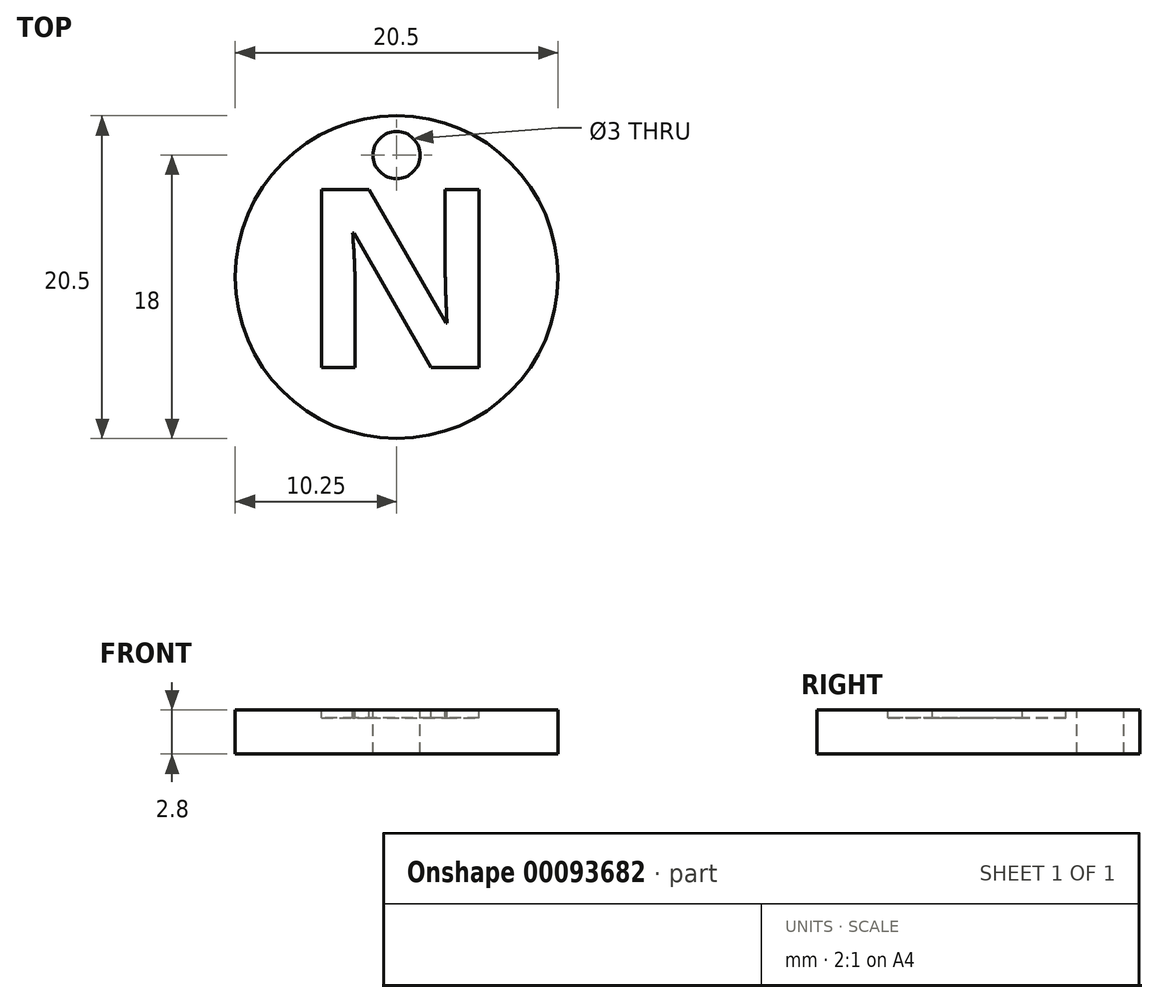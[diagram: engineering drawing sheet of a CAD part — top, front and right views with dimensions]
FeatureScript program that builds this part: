
annotation { "Feature Type Name" : "Feature", "Feature Type Description" : "" }
export const myFeature = defineFeature(function(context is Context, id is Id, definition is map)
    precondition{}
    {
        {
            var Q0;
            Q0=qCreatedBy(makeId("Top.planeOp"),FACE);
            var sketch = newSketch(context, id + "F0", { "sketchPlane" : qUnion([Q0])});
            skCircle(sketch, "E0", {"center": v(0, 0) * mm, "radius": 10.25 * mm});
            skSolve(sketch);
        }
        {
            var Q0;
            Q0=makeQuery(id+"F0.imprint","IMPRINT",FACE,{"disambiguationData":[TD([[makeQuery(id+"F0.imprint","IMPRINT",EDGE,{"derivedFrom":sQuery(id+"F0.wireOp",EDGE,"E0")}),1.0]])]});
            extrude(context, id + "F1", {"entities" : qUnion([Q0]), "depth" : 2.8 * mm});
        }
        {
            var Q0;
            Q0=makeQuery(id+"F1.opExtrude","CAP_FACE",FACE,{"disambiguationData":[OSD([sQuery(id+"F0.wireOp",EDGE,"E0")])],"isStart":false});
            var sketch = newSketch(context, id + "F2", { "sketchPlane" : qUnion([Q0])});
            skText(sketch, "E1", { "text": "N", "fontName": "OpenSans-Bold.ttf"});
            const initialGuessF2  = {"E1": [-0.0062, -0.00574, 1, 0, 0.0114]};
            skSetInitialGuess(sketch, initialGuessF2);
            skSolve(sketch);
        }
        {
            var Q0;
            Q0=makeQuery(id+"F2.imprint","IMPRINT",FACE,{"disambiguationData":[TD([[makeQuery(id+"F2.imprint","IMPRINT",EDGE,{"derivedFrom":sQuery(id+"F2.wireOp",EDGE,"E1.sketch_text.stroke-0")}),-1.0]])]});
            extrude(context, id + "F3", {"entities" : qUnion([Q0]), "operationType" : NewBodyOperationType.REMOVE, "oppositeDirection" : true, "depth" : .5 * mm});
        }
        {
            var Q0;
            Q0=makeQuery(id+"F1.opExtrude","CAP_FACE",FACE,{"disambiguationData":[OSD([sQuery(id+"F0.wireOp",EDGE,"E0")])],"isStart":false});
            var sketch = newSketch(context, id + "F4", { "sketchPlane" : qUnion([Q0])});
            skCircle(sketch, "E2", {"center": v(0, 7.75) * mm, "radius": 1.5 * mm});
            skSolve(sketch);
        }
        {
            var Q0;
            Q0=makeQuery(id+"F4.imprint","IMPRINT",FACE,{"disambiguationData":[TD([[makeQuery(id+"F4.imprint","IMPRINT",EDGE,{"derivedFrom":sQuery(id+"F4.wireOp",EDGE,"E2")}),1.0]])]});
            extrude(context, id + "F5", {"entities" : qUnion([Q0]), "operationType" : NewBodyOperationType.REMOVE, "oppositeDirection" : true, "depth" : 25 * mm});
        }
    });
